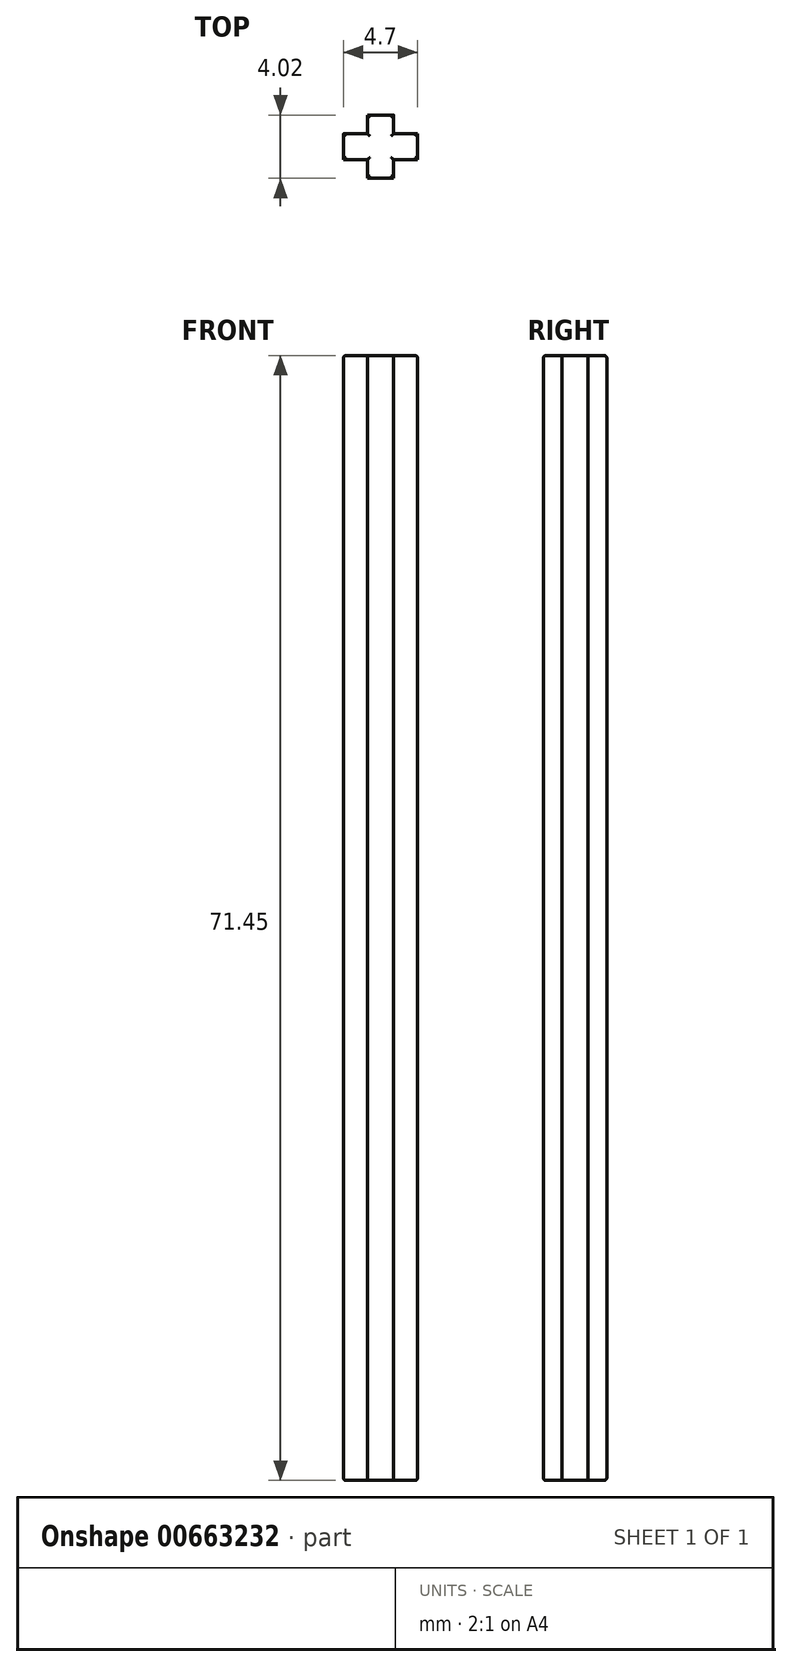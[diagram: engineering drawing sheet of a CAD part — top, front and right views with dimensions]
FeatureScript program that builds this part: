
annotation { "Feature Type Name" : "Feature", "Feature Type Description" : "" }
export const myFeature = defineFeature(function(context is Context, id is Id, definition is map)
    precondition{}
    {
        {
            var Q0;
            Q0=qCreatedBy(makeId("Top.planeOp"),FACE);
            var sketch = newSketch(context, id + "F0", { "sketchPlane" : qUnion([Q0])});
            skLineSegment(sketch, "E0.bottom", {"start": v(0.83, 2) * mm, "end": v(-0.83, 2) * mm});
            skLineSegment(sketch, "E0.top", {"start": v(0.83, -2) * mm, "end": v(-0.83, -2) * mm});
            skLineSegment(sketch, "E0.left", {"start": v(0.83, 2) * mm, "end": v(0.83, -2) * mm});
            skLineSegment(sketch, "E0.right", {"start": v(-0.83, 2) * mm, "end": v(-0.83, -2) * mm});
            skPoint(sketch, "E0.middle", {"position": v(0, 0) * mm});
            skLineSegment(sketch, "E1.bottom", {"start": v(2.35, -0.83) * mm, "end": v(-2.35, -0.83) * mm});
            skLineSegment(sketch, "E1.top", {"start": v(2.35, 0.83) * mm, "end": v(-2.35, 0.83) * mm});
            skLineSegment(sketch, "E1.left", {"start": v(2.35, -0.83) * mm, "end": v(2.35, 0.83) * mm});
            skLineSegment(sketch, "E1.right", {"start": v(-2.35, -0.83) * mm, "end": v(-2.35, 0.83) * mm});
            skSolve(sketch);
        }
        {
            var Q0;
            Q0 = qSketchRegion(id + "F0", true);
            extrude(context, id + "F1", {"entities" : qUnion([Q0]), "depth" : 71.45 * mm, "offsetDistance" : 25 * mm});
        }
        {
            var Q0;
            Q0=makeQuery(id+"F1.opExtrude","CAP_EDGE",EDGE,{"disambiguationData":[OSD([sQuery(id+"F0.wireOp",EDGE,"E1.right")])],"isStart":false});
            var Q1;
            {var subQ0=sQuery(id+"F0.wireOp",EDGE,"E1.top");Q1=makeQuery(id+"F1.opExtrude","CAP_EDGE",EDGE,{"disambiguationData":[OSD([subQ0]),TDD([makeQuery(id+"F0.imprint","IMPRINT",EDGE,{"disambiguationData":[TD([[makeQuery(id+"F0.imprint","INTERSECT",VERTEX,{"derivedFrom":[sQuery(id+"F0.wireOp",EDGE,"E0.right"),subQ0]}),-1.0]])],"derivedFrom":subQ0})])],"isStart":false});}
            var Q2;
            {var subQ0=sQuery(id+"F0.wireOp",EDGE,"E0.right");Q2=makeQuery(id+"F1.opExtrude","CAP_EDGE",EDGE,{"disambiguationData":[OSD([subQ0]),TDD([makeQuery(id+"F0.imprint","IMPRINT",EDGE,{"disambiguationData":[TD([[makeQuery(id+"F0.imprint","INTERSECT",VERTEX,{"derivedFrom":[sQuery(id+"F0.wireOp",EDGE,"E0.bottom"),subQ0]}),-1.0]])],"derivedFrom":subQ0})])],"isStart":false});}
            var Q3;
            Q3=makeQuery(id+"F1.opExtrude","CAP_EDGE",EDGE,{"disambiguationData":[OSD([sQuery(id+"F0.wireOp",EDGE,"E0.bottom")])],"isStart":false});
            var Q4;
            {var subQ0=sQuery(id+"F0.wireOp",EDGE,"E0.left");Q4=makeQuery(id+"F1.opExtrude","CAP_EDGE",EDGE,{"disambiguationData":[OSD([subQ0]),TDD([makeQuery(id+"F0.imprint","IMPRINT",EDGE,{"disambiguationData":[TD([[makeQuery(id+"F0.imprint","INTERSECT",VERTEX,{"derivedFrom":[sQuery(id+"F0.wireOp",EDGE,"E0.bottom"),subQ0]}),-1.0]])],"derivedFrom":subQ0})])],"isStart":false});}
            var Q5;
            Q5=makeQuery(id+"F1.opExtrude","CAP_EDGE",EDGE,{"disambiguationData":[OSD([sQuery(id+"F0.wireOp",EDGE,"E1.left")])],"isStart":false});
            var Q6;
            {var subQ0=sQuery(id+"F0.wireOp",EDGE,"E1.top");Q6=makeQuery(id+"F1.opExtrude","CAP_EDGE",EDGE,{"disambiguationData":[OSD([subQ0]),TDD([makeQuery(id+"F0.imprint","IMPRINT",EDGE,{"disambiguationData":[TD([[makeQuery(id+"F0.imprint","INTERSECT",VERTEX,{"derivedFrom":[sQuery(id+"F0.wireOp",EDGE,"E0.left"),subQ0]}),1.0]])],"derivedFrom":subQ0})])],"isStart":false});}
            var Q7;
            {var subQ0=sQuery(id+"F0.wireOp",EDGE,"E1.bottom");Q7=makeQuery(id+"F1.opExtrude","CAP_EDGE",EDGE,{"disambiguationData":[OSD([subQ0]),TDD([makeQuery(id+"F0.imprint","IMPRINT",EDGE,{"disambiguationData":[TD([[makeQuery(id+"F0.imprint","INTERSECT",VERTEX,{"derivedFrom":[sQuery(id+"F0.wireOp",EDGE,"E0.left"),subQ0]}),1.0]])],"derivedFrom":subQ0})])],"isStart":false});}
            var Q8;
            {var subQ0=sQuery(id+"F0.wireOp",EDGE,"E0.left");Q8=makeQuery(id+"F1.opExtrude","CAP_EDGE",EDGE,{"disambiguationData":[OSD([subQ0]),TDD([makeQuery(id+"F0.imprint","IMPRINT",EDGE,{"disambiguationData":[TD([[makeQuery(id+"F0.imprint","INTERSECT",VERTEX,{"derivedFrom":[sQuery(id+"F0.wireOp",EDGE,"E0.top"),subQ0]}),1.0]])],"derivedFrom":subQ0})])],"isStart":false});}
            var Q9;
            Q9=makeQuery(id+"F1.opExtrude","CAP_EDGE",EDGE,{"disambiguationData":[OSD([sQuery(id+"F0.wireOp",EDGE,"E0.top")])],"isStart":false});
            var Q10;
            {var subQ0=sQuery(id+"F0.wireOp",EDGE,"E0.right");Q10=makeQuery(id+"F1.opExtrude","CAP_EDGE",EDGE,{"disambiguationData":[OSD([subQ0]),TDD([makeQuery(id+"F0.imprint","IMPRINT",EDGE,{"disambiguationData":[TD([[makeQuery(id+"F0.imprint","INTERSECT",VERTEX,{"derivedFrom":[sQuery(id+"F0.wireOp",EDGE,"E0.top"),subQ0]}),1.0]])],"derivedFrom":subQ0})])],"isStart":false});}
            var Q11;
            {var subQ0=sQuery(id+"F0.wireOp",EDGE,"E1.bottom");Q11=makeQuery(id+"F1.opExtrude","CAP_EDGE",EDGE,{"disambiguationData":[OSD([subQ0]),TDD([makeQuery(id+"F0.imprint","IMPRINT",EDGE,{"disambiguationData":[TD([[makeQuery(id+"F0.imprint","INTERSECT",VERTEX,{"derivedFrom":[subQ0,sQuery(id+"F0.wireOp",EDGE,"E1.right")]}),1.0]])],"derivedFrom":subQ0})])],"isStart":false});}
            fillet(context, id + "F2", {"entities" : qUnion([Q0, Q1, Q2, Q3, Q4, Q5, Q6, Q7, Q8, Q9, Q10, Q11]), "tangentPropagation" : true, "radius" : 0.15 * mm, "defaultsChanged" : false, "vertexSettings" : [], "allowEdgeOverflow" : false});
        }
        {
            var Q0;
            {var subQ0=sQuery(id+"F0.wireOp",EDGE,"E1.bottom");Q0=makeQuery(id+"F1.opExtrude","CAP_EDGE",EDGE,{"disambiguationData":[OSD([subQ0]),TDD([makeQuery(id+"F0.imprint","IMPRINT",EDGE,{"disambiguationData":[TD([[makeQuery(id+"F0.imprint","INTERSECT",VERTEX,{"derivedFrom":[subQ0,sQuery(id+"F0.wireOp",EDGE,"E1.right")]}),1.0]])],"derivedFrom":subQ0})])],"isStart":true});}
            var Q1;
            Q1=makeQuery(id+"F1.opExtrude","CAP_EDGE",EDGE,{"disambiguationData":[OSD([sQuery(id+"F0.wireOp",EDGE,"E1.right")])],"isStart":true});
            var Q2;
            {var subQ0=sQuery(id+"F0.wireOp",EDGE,"E1.top");Q2=makeQuery(id+"F1.opExtrude","CAP_EDGE",EDGE,{"disambiguationData":[OSD([subQ0]),TDD([makeQuery(id+"F0.imprint","IMPRINT",EDGE,{"disambiguationData":[TD([[makeQuery(id+"F0.imprint","INTERSECT",VERTEX,{"derivedFrom":[sQuery(id+"F0.wireOp",EDGE,"E0.right"),subQ0]}),-1.0]])],"derivedFrom":subQ0})])],"isStart":true});}
            var Q3;
            {var subQ0=sQuery(id+"F0.wireOp",EDGE,"E0.right");Q3=makeQuery(id+"F1.opExtrude","CAP_EDGE",EDGE,{"disambiguationData":[OSD([subQ0]),TDD([makeQuery(id+"F0.imprint","IMPRINT",EDGE,{"disambiguationData":[TD([[makeQuery(id+"F0.imprint","INTERSECT",VERTEX,{"derivedFrom":[sQuery(id+"F0.wireOp",EDGE,"E0.bottom"),subQ0]}),-1.0]])],"derivedFrom":subQ0})])],"isStart":true});}
            var Q4;
            Q4=makeQuery(id+"F1.opExtrude","CAP_EDGE",EDGE,{"disambiguationData":[OSD([sQuery(id+"F0.wireOp",EDGE,"E0.bottom")])],"isStart":true});
            var Q5;
            {var subQ0=sQuery(id+"F0.wireOp",EDGE,"E0.left");Q5=makeQuery(id+"F1.opExtrude","CAP_EDGE",EDGE,{"disambiguationData":[OSD([subQ0]),TDD([makeQuery(id+"F0.imprint","IMPRINT",EDGE,{"disambiguationData":[TD([[makeQuery(id+"F0.imprint","INTERSECT",VERTEX,{"derivedFrom":[sQuery(id+"F0.wireOp",EDGE,"E0.bottom"),subQ0]}),-1.0]])],"derivedFrom":subQ0})])],"isStart":true});}
            var Q6;
            {var subQ0=sQuery(id+"F0.wireOp",EDGE,"E1.top");Q6=makeQuery(id+"F1.opExtrude","CAP_EDGE",EDGE,{"disambiguationData":[OSD([subQ0]),TDD([makeQuery(id+"F0.imprint","IMPRINT",EDGE,{"disambiguationData":[TD([[makeQuery(id+"F0.imprint","INTERSECT",VERTEX,{"derivedFrom":[sQuery(id+"F0.wireOp",EDGE,"E0.left"),subQ0]}),1.0]])],"derivedFrom":subQ0})])],"isStart":true});}
            var Q7;
            Q7=makeQuery(id+"F1.opExtrude","CAP_EDGE",EDGE,{"disambiguationData":[OSD([sQuery(id+"F0.wireOp",EDGE,"E1.left")])],"isStart":true});
            var Q8;
            {var subQ0=sQuery(id+"F0.wireOp",EDGE,"E1.bottom");Q8=makeQuery(id+"F1.opExtrude","CAP_EDGE",EDGE,{"disambiguationData":[OSD([subQ0]),TDD([makeQuery(id+"F0.imprint","IMPRINT",EDGE,{"disambiguationData":[TD([[makeQuery(id+"F0.imprint","INTERSECT",VERTEX,{"derivedFrom":[sQuery(id+"F0.wireOp",EDGE,"E0.left"),subQ0]}),1.0]])],"derivedFrom":subQ0})])],"isStart":true});}
            var Q9;
            {var subQ0=sQuery(id+"F0.wireOp",EDGE,"E0.left");Q9=makeQuery(id+"F1.opExtrude","CAP_EDGE",EDGE,{"disambiguationData":[OSD([subQ0]),TDD([makeQuery(id+"F0.imprint","IMPRINT",EDGE,{"disambiguationData":[TD([[makeQuery(id+"F0.imprint","INTERSECT",VERTEX,{"derivedFrom":[sQuery(id+"F0.wireOp",EDGE,"E0.top"),subQ0]}),1.0]])],"derivedFrom":subQ0})])],"isStart":true});}
            var Q10;
            Q10=makeQuery(id+"F1.opExtrude","CAP_EDGE",EDGE,{"disambiguationData":[OSD([sQuery(id+"F0.wireOp",EDGE,"E0.top")])],"isStart":true});
            var Q11;
            {var subQ0=sQuery(id+"F0.wireOp",EDGE,"E0.right");Q11=makeQuery(id+"F1.opExtrude","CAP_EDGE",EDGE,{"disambiguationData":[OSD([subQ0]),TDD([makeQuery(id+"F0.imprint","IMPRINT",EDGE,{"disambiguationData":[TD([[makeQuery(id+"F0.imprint","INTERSECT",VERTEX,{"derivedFrom":[sQuery(id+"F0.wireOp",EDGE,"E0.top"),subQ0]}),1.0]])],"derivedFrom":subQ0})])],"isStart":true});}
            fillet(context, id + "F3", {"entities" : qUnion([Q0, Q1, Q2, Q3, Q4, Q5, Q6, Q7, Q8, Q9, Q10, Q11]), "tangentPropagation" : true, "radius" : 0.15 * mm, "defaultsChanged" : false, "vertexSettings" : [], "allowEdgeOverflow" : false});
        }
    });
